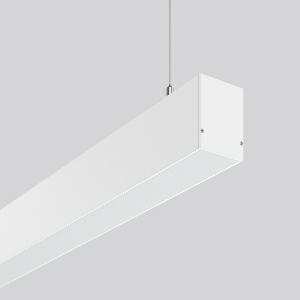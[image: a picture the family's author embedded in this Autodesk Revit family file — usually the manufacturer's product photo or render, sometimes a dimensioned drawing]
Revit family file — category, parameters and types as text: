
# Revit family: less_is_more_50_312321_002_1_2a80
name_source: partatom
category: Lighting Fixtures
units: mm (PartAtom-declared; Revit-internal decimal feet)

## family parameters
Cut with Voids When Loaded = No
Host = Face
Light Source = No
Part Type = Normal
Room Calculation Point = No
Round Connector Dimension = Use Diameter
Shared = No

## types (1)
- LESS IS MORE 50 (1 x LED Modul 840, 8850 lm, 4000)
    Apparent Load = 74 VA
    CIE Flux Codes = 49 80 96 63 100
    Color Rendering = 80
    Color Temperature = 4000
    Default Elevation = 1800 mm
    Description = Series: LESS IS MORE 50
Linear pendant luminaire for aesthetically sophisticated lighting. Housing: extruded aluminium profile, powder-coated. End cap aluminium powder-coated. Canopy made of aluminium, powder-coated. Diffuser made of non-yellowing plastic (PMMA), opal. Direct 65%, indirect 35% light emission. Suitable for pendant. 2-point steel cable suspension freely positionable and infinitely height-adjustable. Special lengths available on request. LED unit with integrated converter interchangeable and removable. Suitable for through-wiring. With sensors or as a safety luminaire on request. 
Colour: traffic white, matt (RAL 9016)
Length: 1967 mm
Width: 57 mm
Height: 75 mm
Suspension length: 2000 mm
Lamp: LED
Socket: without socket
Colour temperature: 4000K
Colour rendering index (CRI): 80
Light source: LED
Socket lamp2: Without base
Colour temperature: 4000K
System power: 74 W
Rated luminous flux: 8850 lm
Luminous efficiency: 120 lm/W
Control gear: Regulated power supply
Control gear: Regulated power supply
Protection class: I
Type of protection: IP 20
    Height = 75 mm
    Lamp = 1 x LED Modul 840
    Lamp Light Flux = 8850 lm
    Lamp count = 1
    Length = 1967 mm
    Lifetime = 50000 h
    Luminous efficacy = 120 lm/W
    Manufacturer = RZB
    ModVariant = No
    Model = 312321.002.1
    Mounting Place = Ceiling
    Mounting Type = Pendant
    Number of Poles = 1
    OnlyDefault = Yes
    Power Factor = 1
    Product Name = LESS IS MORE 50
    Product group = Pendant LED linear luminaires
    ProductGroupID = 907
    Protection Class = Protection class I
    Protection Degree = IP 20
    RLX_Detail_Level = 1
    RLX_Emergency_Light_Flux = 0 lm
    RLX_Emergency_Type = 0
    RLX_Emergency_Type_DB = No
    RlxData = <blob elided: 31605 chars, md5=bd82d4ab>
    Socket = socket
    Standby Power = 0 W
    System Light Flux = 8850 lm
    System Power = 74 W
    Type Comments = Product without accessories
    Type Image = 312318.002.jpg
    URL = http://relux.com
    VarID = ---
    Voltage = 230 V
    Voltage Range = 220-240 V
    Weight = 0.00 kg
    Width = 57 mm

## geometry (parser evidence)
native form markers: Blend x4, Sweep x11
no freeform markers — native parametric forms only
